# Revit family: Stormbell 80 Wellbeing
name_source: partatom
category: Lighting Fixtures
revit_build: Autodesk Revit 2018 (Build: 20170223_1515(x64)
units: mm (PartAtom-declared; Revit-internal decimal feet)

## family parameters
Cut with Voids When Loaded = No
Host = Face
Light Source = Yes
Part Type = Normal
Room Calculation Point = No
Round Connector Dimension = Use Diameter
Shared = No

## types (1)
- Stormbell 80 Wellbeing
    Apparent Load = 14 VA
    Black = Texturized Black RAL 9011
    Bottom ring Height = 686 mm
    CRI = 90
    Color Filter = 16777215
    Cork = Cork
    Default Elevation = 1219 mm
    Description = STORMBELL 80 pendant downlight by Lamp.
Body made of die-cast aluminium finished in WHITE, BLACK or MATERIALITY colour palette, with black or
opal polycarbonate ring, for decorative lighting effect and possibility of colour filter accessory, depending on
model.
Static colour temperature 3000K, 4000K with CRI90. Also available in Wellbeing technology with optimised
light spectrum in 480 nm emissions for maximum circadian stimulation, available in 3000K and 4000K, with
CRI above 95. Choice of models with dynamic colour temperature (2700-6500K).
Aluminium reflector available in various apertures: SPOT, MEDIUM FLOOD and WIDE FLOOD.
Luminaire with various installation possibilities: suspended or recessed ceiling canopy with electronic wiring
included, ON/OFF or DALI. Possibility of Bluetooth LE control. Suspended installation option with track
adapter, compatible with NOMADIC SYSTEM.
Insulation class I. Lifetime: 50000 L90 B10.
Compatible with 4 different models of bells (accessories) that complete the luminaire, in WHITE, BLACK or
MATERIALITY colour palette, as well.
    Diameter = 86 mm
    Dimming Lamp Color Temperature Shift = <None>
    Driver is required = Yes
    Finish = Please consult the type parameters 'Reflector Accesory  Finish' and 'Set Finish'
    Height = 88 mm
    Installation instructions = https://www.lamp.es
    LED Lifetime = 50.000 L90 B10
    Last update = 25-08-2022
    Lm LED = 1500 lm
    Lookup Table Name = Stormbell80
    Luminaire type = Hanging luminaire
    MacAdam = 3
    Main body Height = 76 mm
    Manufacturer = LAMP
    Manufacturer URL = https://www.lamp.es
    Manufacturer country = Spain
    Manufacturer name = LAMP
    Materiality 1 = Texturized Materiality RAL 1013
    Materiality 2 = Texturized Materiality RAL 5008
    Materiality 3 = Texturized Materiality S3010
    Materiality 4 = Texturized Materiality S2010
    Materiality 5 = Texturized Materiality S4050
    Max Luminaire Drop Length by Manufacturer = 2000 mm
    Model = Please consult the instance parameters related to the code configuration
    Number of poles = 2
    Optics Code Definition = 1
    PET = recycled PET plastic grey
    Photometric Web File = ST18XXLOSP9XXXXX.IES
    Power = 14 W
    Product Code = Please consult the instance parameters related to the code configuration
    Product URL = https://www.lamp.es
    Product datasheet = https://www.lamp.es
    Rosette Finish = Texturized Black RAL 9011
    Tilt Angle = 90.00°
    Top ring Height = 5 mm  [stored 0.0164042 ft]
    Type Image = default.jpg
    URL = https://www.lamp.es
    Weight = 0.80 kg
    White = Texturized White RAL 9010

note: [stored X ft] marks values corroborated as IEEE doubles in the binary element streams (Revit-internal decimal feet)

## geometry (parser evidence)
native form markers: Sweep x14
no freeform markers — native parametric forms only
